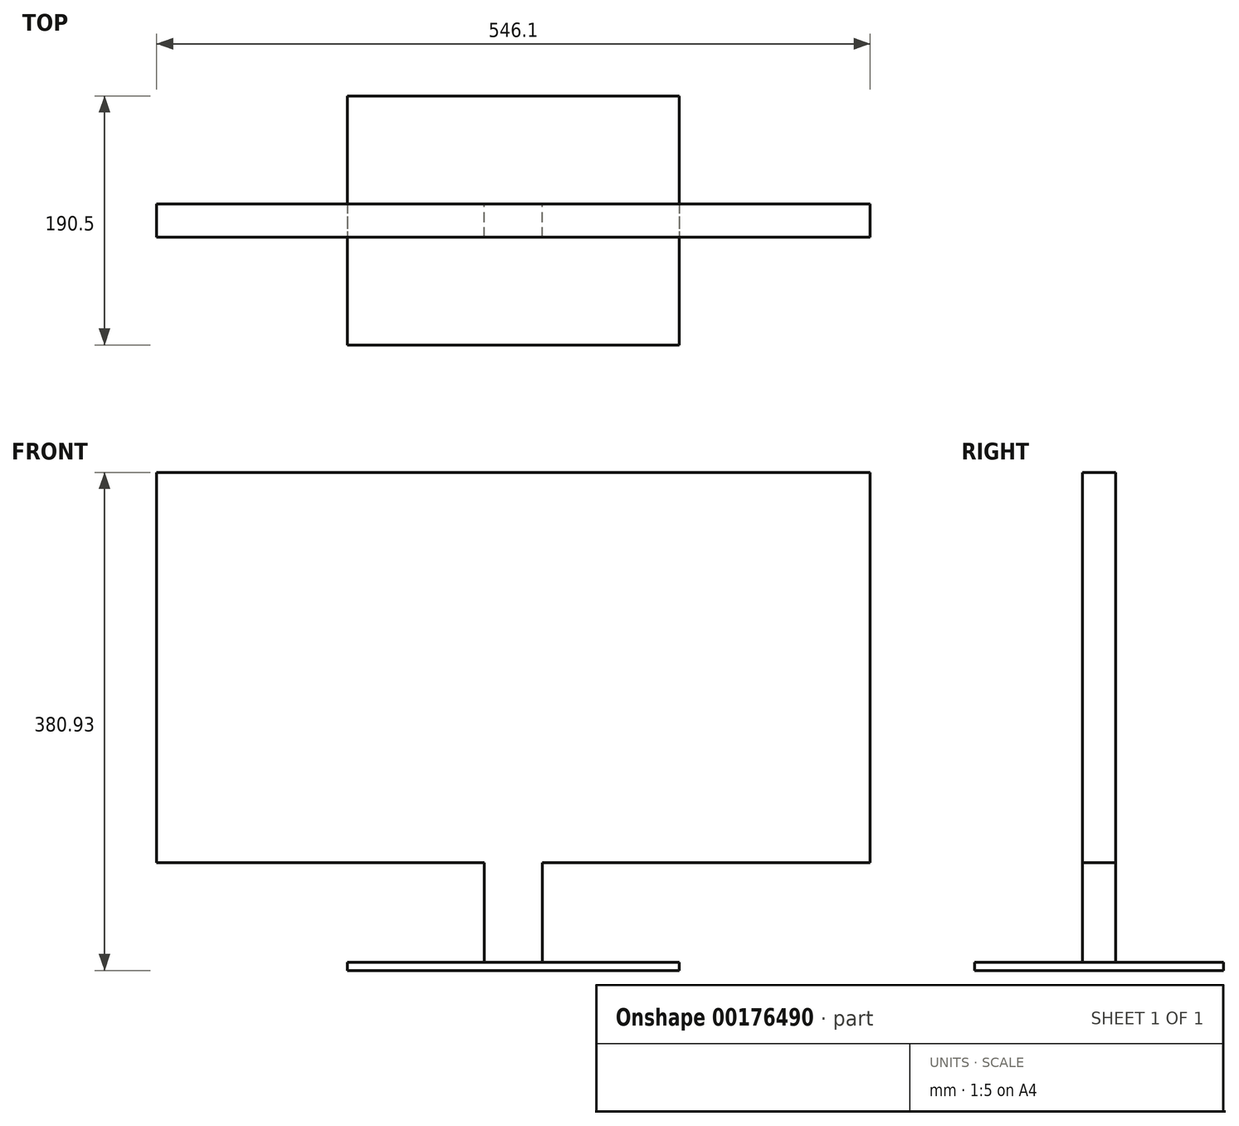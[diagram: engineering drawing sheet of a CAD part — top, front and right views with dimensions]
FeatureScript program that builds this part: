
annotation { "Feature Type Name" : "Feature", "Feature Type Description" : "" }
export const myFeature = defineFeature(function(context is Context, id is Id, definition is map)
    precondition{}
    {
        {
            var Q0;
            Q0=qCreatedBy(makeId("Front.planeOp"),FACE);
            var sketch = newSketch(context, id + "F0", { "sketchPlane" : qUnion([Q0])});
            skLineSegment(sketch, "E0.bottom", {"start": v(273.05, 149.2) * mm, "end": v(-273.05, 149.2) * mm});
            skLineSegment(sketch, "E0.top", {"start": v(273.05, -149.2) * mm, "end": v(-273.05, -149.2) * mm});
            skLineSegment(sketch, "E0.left", {"start": v(273.05, 149.2) * mm, "end": v(273.05, -149.2) * mm});
            skLineSegment(sketch, "E0.right", {"start": v(-273.05, 149.2) * mm, "end": v(-273.05, -149.2) * mm});
            skPoint(sketch, "E0.middle", {"position": v(0, 0) * mm});
            skLineSegment(sketch, "E1", {"start": v(-273.05, 149.2) * mm, "end": v(273.05, -149.2) * mm});
            skLineSegment(sketch, "E2.top", {"start": v(22.23, -225.4) * mm, "end": v(-22.22, -225.4) * mm});
            skLineSegment(sketch, "E2.left", {"start": v(22.23, -149.2) * mm, "end": v(22.23, -225.4) * mm});
            skLineSegment(sketch, "E2.right", {"start": v(-22.22, -149.2) * mm, "end": v(-22.22, -225.4) * mm});
            skPoint(sketch, "E2.middle", {"position": v(0, -149.2) * mm});
            skSolve(sketch);
        }
        {
            var Q0;
            Q0 = qSketchRegion(id + "F0", true);
            extrude(context, id + "F1", {"entities" : qUnion([Q0]), "endBound" : BoundingType.SYMMETRIC, "depth" : 25.4 * mm});
        }
        {
            var Q0;
            Q0=makeQuery(id+"F1.opExtrude","SWEPT_FACE",FACE,{"disambiguationData":[OSD([sQuery(id+"F0.wireOp",EDGE,"E2.top")])]});
            var sketch = newSketch(context, id + "F2", { "sketchPlane" : qUnion([Q0])});
            skLineSegment(sketch, "E3.bottom", {"start": v(127, -95.25) * mm, "end": v(-127, -95.25) * mm});
            skLineSegment(sketch, "E3.top", {"start": v(127, 95.25) * mm, "end": v(-127, 95.25) * mm});
            skLineSegment(sketch, "E3.left", {"start": v(127, -95.25) * mm, "end": v(127, 95.25) * mm});
            skLineSegment(sketch, "E3.right", {"start": v(-127, -95.25) * mm, "end": v(-127, 95.25) * mm});
            skPoint(sketch, "E3.middle", {"position": v(0, 0) * mm});
            skSolve(sketch);
        }
        {
            var Q0;
            Q0 = qSketchRegion(id + "F2", true);
            extrude(context, id + "F3", {"entities" : qUnion([Q0]), "operationType" : NewBodyOperationType.ADD, "depth" : 6.35 * mm});
        }
    });
